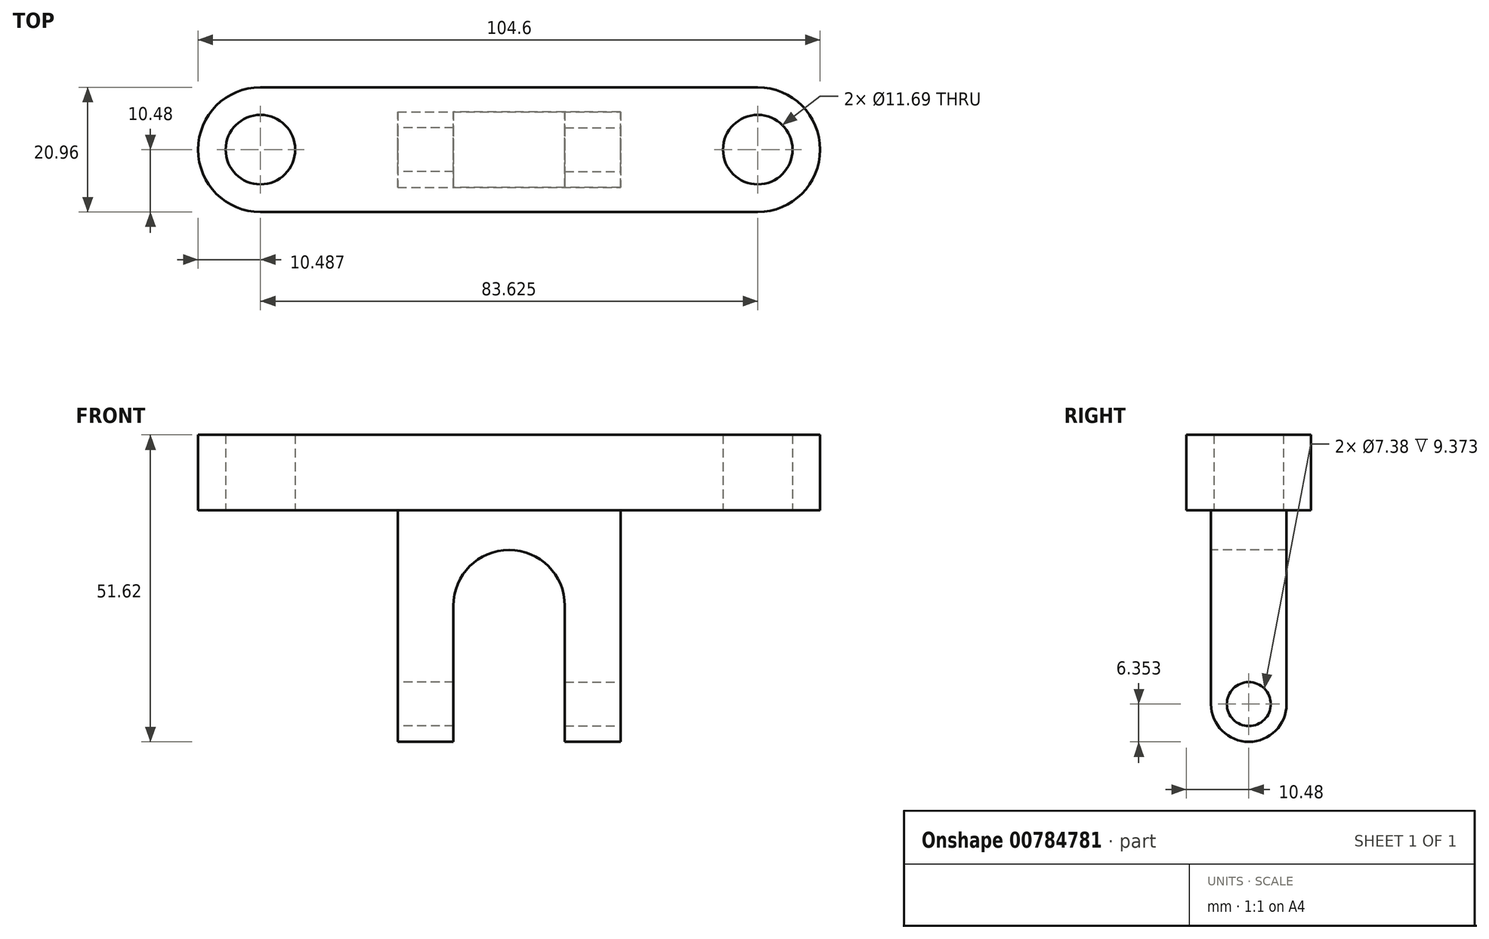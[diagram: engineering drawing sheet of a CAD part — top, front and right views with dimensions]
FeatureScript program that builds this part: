
annotation { "Feature Type Name" : "Feature", "Feature Type Description" : "" }
export const myFeature = defineFeature(function(context is Context, id is Id, definition is map)
    precondition{}
    {
        {
            var Q0;
            Q0=qCreatedBy(makeId("Top.planeOp"),FACE);
            var sketch = newSketch(context, id + "F0", { "sketchPlane" : qUnion([Q0])});
            skLineSegment(sketch, "E0.left", {"start": v(0, 10.48) * mm, "end": v(0, -10.48) * mm});
            skLineSegment(sketch, "E1.MirrorCS", {"start": v(0, 10.48) * mm, "end": v(41.81, 10.48) * mm});
            skLineSegment(sketch, "E2.MirrorCS", {"start": v(0, -10.48) * mm, "end": v(41.81, -10.48) * mm});
            skArc(sketch, "E3.MirrorCS", {"start": v(41.81, 10.48) * mm, "mid": v(52.3, 0) * mm, "end": v(41.81, -10.48) * mm});
            skCircle(sketch, "E4.MirrorC", {"center": v(41.81, 0) * mm, "radius": 5.85 * mm});
            skSolve(sketch);
        }
        {
            var Q0;
            Q0=makeQuery(id+"F0.imprint","IMPRINT",FACE,{"disambiguationData":[TD([[makeQuery(id+"F0.imprint","IMPRINT",EDGE,{"derivedFrom":sQuery(id+"F0.wireOp",EDGE,"E0.left")}),1.0]])]});
            var Q1;
            {var subQ2=sQuery(id+"F0.wireOp",EDGE,"E0.bottom");Q1=makeQuery(id+"F0.imprint","IMPRINT",FACE,{"disambiguationData":[TD([[makeQuery(id+"F0.imprint","IMPRINT",EDGE,{"derivedFrom":subQ2}),1.0]])]});}
            var Q2;
            {var subQ0=sQuery(id+"F0.wireOp",EDGE,"Gsxaz7jW-qDZL-wSsL-FccB-TSJWO8udVrlF");Q2=makeQuery(id+"F0.imprint","IMPRINT",FACE,{"disambiguationData":[TD([[makeQuery(id+"F0.imprint","IMPRINT",EDGE,{"derivedFrom":subQ0}),1.0]])]});}
            extrude(context, id + "F1", {"entities" : qUnion([Q0, Q1, Q2]), "depth" : 12.7 * mm, "offsetDistance" : 25.4 * mm});
        }
        {
            var Q0;
            Q0=qCreatedBy(makeId("Front.planeOp"),FACE);
            var sketch = newSketch(context, id + "F2", { "sketchPlane" : qUnion([Q0])});
            skLineSegment(sketch, "E5", {"start": v(0, 0) * mm, "end": v(18.73, 0) * mm});
            skLineSegment(sketch, "E6", {"start": v(18.73, 0) * mm, "end": v(18.73, -32.57) * mm});
            skLineSegment(sketch, "E7", {"start": v(18.73, -32.57) * mm, "end": v(9.37, -32.57) * mm});
            skPoint(sketch, "E7.endSnap0", {"position": v(9.37, 0) * mm});
            skLineSegment(sketch, "E8", {"start": v(9.37, -32.57) * mm, "end": v(9.37, -16.01) * mm});
            skArc(sketch, "E9", {"start": v(9.37, -16.01) * mm, "mid": v(6.62, -9.39) * mm, "end": v(0, -6.65) * mm});
            skLineSegment(sketch, "E10", {"start": v(0, 0) * mm, "end": v(0, -6.65) * mm});
            skSolve(sketch);
        }
        {
            var Q0;
            Q0=makeQuery(id+"F2.imprint","IMPRINT",FACE,{"disambiguationData":[TD([[makeQuery(id+"F2.imprint","IMPRINT",EDGE,{"derivedFrom":sQuery(id+"F2.wireOp",EDGE,"E5")}),-1.0]])]});
            extrude(context, id + "F3", {"entities" : qUnion([Q0]), "operationType" : NewBodyOperationType.ADD, "oppositeDirection" : true, "depth" : 6.35 * mm, "offsetDistance" : 25.4 * mm});
        }
        {
            var Q0;
            Q0=makeQuery(id+"F3.opExtrude","CAP_FACE",FACE,{"disambiguationData":[OSD([sQuery(id+"F2.wireOp",EDGE,"E5"),sQuery(id+"F2.wireOp",EDGE,"E6"),sQuery(id+"F2.wireOp",EDGE,"E7"),sQuery(id+"F2.wireOp",EDGE,"E8"),sQuery(id+"F2.wireOp",EDGE,"E9"),sQuery(id+"F2.wireOp",EDGE,"E10")])],"isStart":true});
            extrude(context, id + "F4", {"entities" : qUnion([Q0]), "operationType" : NewBodyOperationType.ADD, "depth" : 6.35 * mm, "offsetDistance" : 25.4 * mm});
        }
        {
            var Q0;
            {var subQ0=sQuery(id+"F2.wireOp",EDGE,"E6");Q0=makeQuery(id+"F4.boolean.opBoolean","MERGE",FACE,{"derivedFrom":[makeQuery(id+"F3.opExtrude","SWEPT_FACE",FACE,{"disambiguationData":[OSD([subQ0])]}),makeQuery(id+"F4.opExtrude","SWEPT_FACE",FACE,{"disambiguationData":[OSD([subQ0])]})]});}
            var sketch = newSketch(context, id + "F5", { "sketchPlane" : qUnion([Q0])});
            skArc(sketch, "E11", {"start": v(-6.35, -32.57) * mm, "mid": v(0, -38.92) * mm, "end": v(6.35, -32.57) * mm});
            skCircle(sketch, "E12", {"center": v(0, -32.57) * mm, "radius": 3.7 * mm});
            skSolve(sketch);
        }
        {
            var Q0;
            {var subQ0=sQuery(id+"F5.wireOp",EDGE,"E11");Q0=makeQuery(id+"F5.imprint","IMPRINT",FACE,{"disambiguationData":[TD([[makeQuery(id+"F5.imprint","IMPRINT",EDGE,{"derivedFrom":subQ0}),1.0]])]});}
            extrude(context, id + "F6", {"entities" : qUnion([Q0]), "operationType" : NewBodyOperationType.ADD, "oppositeDirection" : true, "depth" : 9.37 * mm, "offsetDistance" : 25.4 * mm});
        }
        {
            var Q0;
            Q0 = qSketchRegion(id + "F5", true);
            extrude(context, id + "F7", {"entities" : qUnion([Q0]), "operationType" : NewBodyOperationType.REMOVE, "oppositeDirection" : true, "depth" : 25.4 * mm, "offsetDistance" : 25.4 * mm});
        }
        {
            var Q0;
            Q0=makeQuery(id+"F1.opExtrude","SWEPT_BODY",BODY,{"disambiguationData":[OSD([sQuery(id+"F0.wireOp",EDGE,"E0.left"),sQuery(id+"F0.wireOp",EDGE,"E1.MirrorCS"),sQuery(id+"F0.wireOp",EDGE,"E2.MirrorCS"),sQuery(id+"F0.wireOp",EDGE,"E3.MirrorCS"),sQuery(id+"F0.wireOp",EDGE,"E4.MirrorC")])]});
            var Q1;
            Q1=qCreatedBy(makeId("Right.planeOp"),FACE);
            mirror(context, id + "F8", {"operationType" : NewBodyOperationType.ADD, "entities" : qUnion([Q0]), "mirrorPlane" : qUnion([Q1])});
        }
    });
